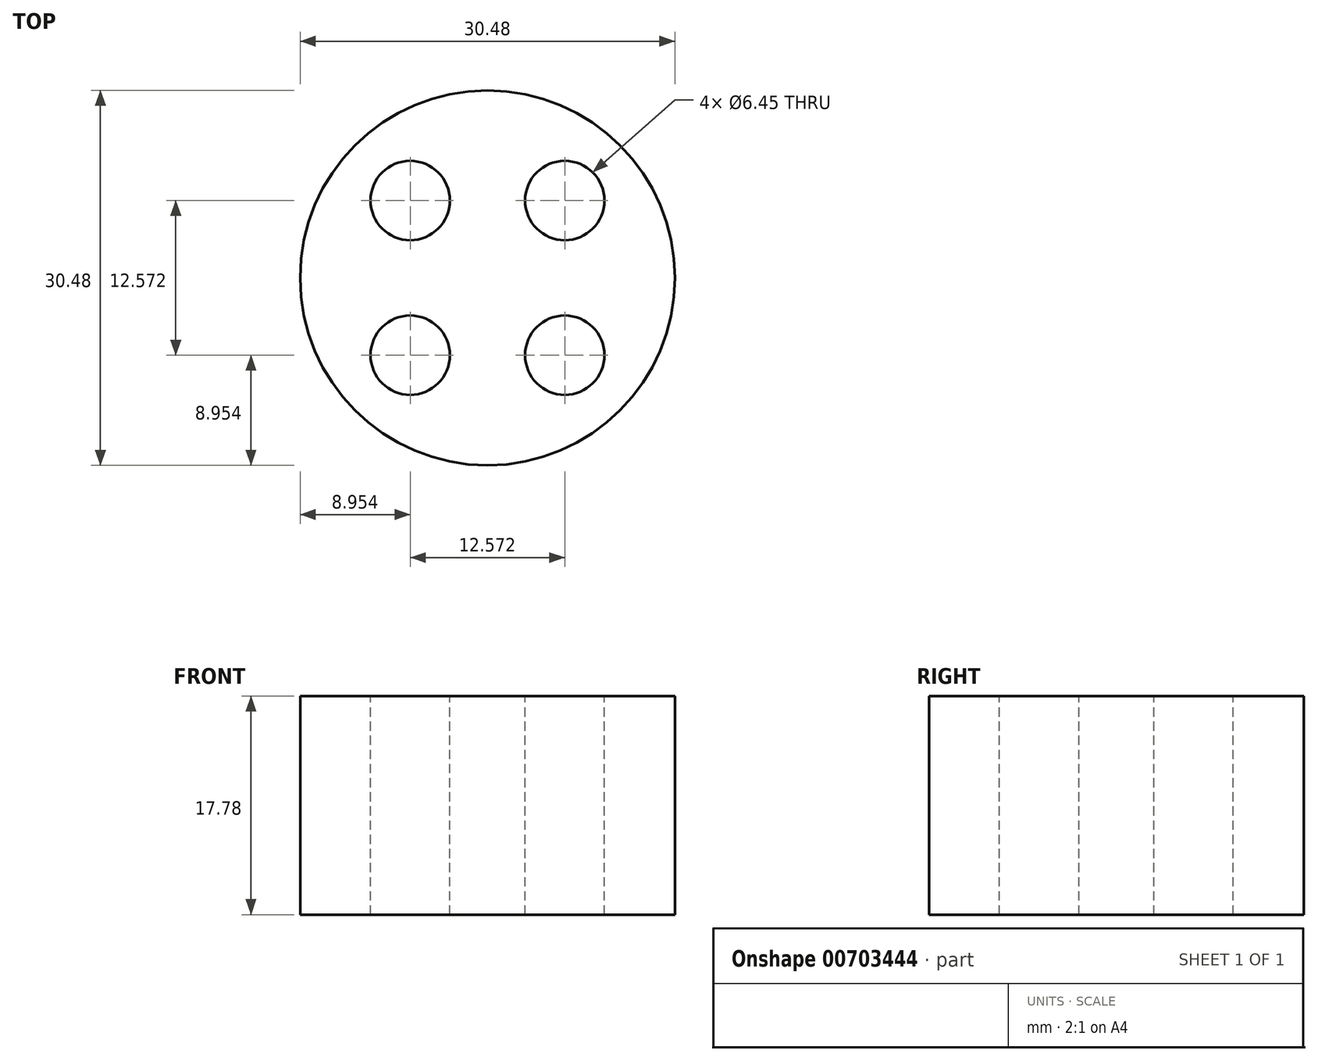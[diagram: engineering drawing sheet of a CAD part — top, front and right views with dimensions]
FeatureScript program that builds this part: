
annotation { "Feature Type Name" : "Feature", "Feature Type Description" : "" }
export const myFeature = defineFeature(function(context is Context, id is Id, definition is map)
    precondition{}
    {
        {
            var Q0;
            Q0=qCreatedBy(makeId("Top.planeOp"),FACE);
            var sketch = newSketch(context, id + "F0", { "sketchPlane" : qUnion([Q0])});
            skCircle(sketch, "E0", {"center": v(0, 0) * mm, "radius": 15.24 * mm});
            skSolve(sketch);
        }
        {
            var Q0;
            Q0=makeQuery(id+"F0.imprint","IMPRINT",FACE,{"disambiguationData":[TD([[makeQuery(id+"F0.imprint","IMPRINT",EDGE,{"derivedFrom":sQuery(id+"F0.wireOp",EDGE,"E0")}),1.0]])]});
            var sketch = newSketch(context, id + "F1", { "sketchPlane" : qUnion([Q0])});
            skCircle(sketch, "E1", {"center": v(6.29, 6.29) * mm, "radius": 3.23 * mm});
            skCircle(sketch, "E2.MirrorC", {"center": v(-6.29, 6.29) * mm, "radius": 3.23 * mm});
            skCircle(sketch, "E3.MirrorC", {"center": v(6.29, -6.29) * mm, "radius": 3.23 * mm});
            skCircle(sketch, "E4.MirrorC", {"center": v(-6.29, -6.29) * mm, "radius": 3.23 * mm});
            skLineSegment(sketch, "E5", {"start": v(0, 18.95) * mm, "end": v(0, -19.2) * mm, "construction": true});
            skLineSegment(sketch, "E6", {"start": v(-20.23, 0) * mm, "end": v(22.64, 0) * mm, "construction": true});
            skLineSegment(sketch, "E7", {"start": v(0, 0) * mm, "end": v(-10.78, 10.78) * mm, "construction": true});
            skPoint(sketch, "E8.middle", {"position": v(0, 0) * mm});
            skSolve(sketch);
        }
        {
            var Q0;
            Q0 = qSketchRegion(id + "F0", true);
            extrude(context, id + "F2", {"entities" : qUnion([Q0]), "endBound" : BoundingType.SYMMETRIC, "depth" : 17.78 * mm, "offsetDistance" : 25.4 * mm});
        }
        {
            var Q0;
            Q0 = qSketchRegion(id + "F1", true);
            extrude(context, id + "F3", {"entities" : qUnion([Q0]), "operationType" : NewBodyOperationType.REMOVE, "endBound" : BoundingType.SYMMETRIC, "oppositeDirection" : true, "depth" : 17.78 * mm, "offsetDistance" : 25.4 * mm});
        }
    });
